# Revit family: Leviton_CATSTD-LP120-XXX-D01
name_source: partatom
category: Electrical Equipment
units: mm (PartAtom-declared; Revit-internal decimal feet)

## family parameters
Always vertical = Yes
Cut with Voids When Loaded = Yes
Host = Wall
Maintain Annotation Orientation = No
Panel Configuration = Two Columns, Circuits Across
Part Type = Panelboard
Room Calculation Point = No
Round Connector Dimension = Use Diameter
Shared = No

## types (1)
- LP120 ASSY
    Cost = 1 $
    Default Elevation = 0 "
    Description = LP120 ASSY - 12 Space Outdoor Solar Ready Meter Main Combo Load Center
    Dimensions = 34.984" H x 14.807" W x 7.299" D
    Ground Bus = No
    Manufacturer = Leviton
    Model = LP120 ASSY
    NEMA Enclosure Type = NEMA 3R
    Neutral Bus = No
    Neutral Rating = 0.00%
    Number of Pole = 1
    Overall Width = 16.803 "
    Product Data = https://www.arcat.com
    Specification = https://www.arcat.com
    URL = https://www.leviton.com
    Unit Depth = 7.299 "
    Unit Height = 34.984 "
    Unit Width = 14.807 "
    Voltage_MEP = 120 V

## geometry (parser evidence)
native form markers: Sweep x4
no freeform markers — native parametric forms only
